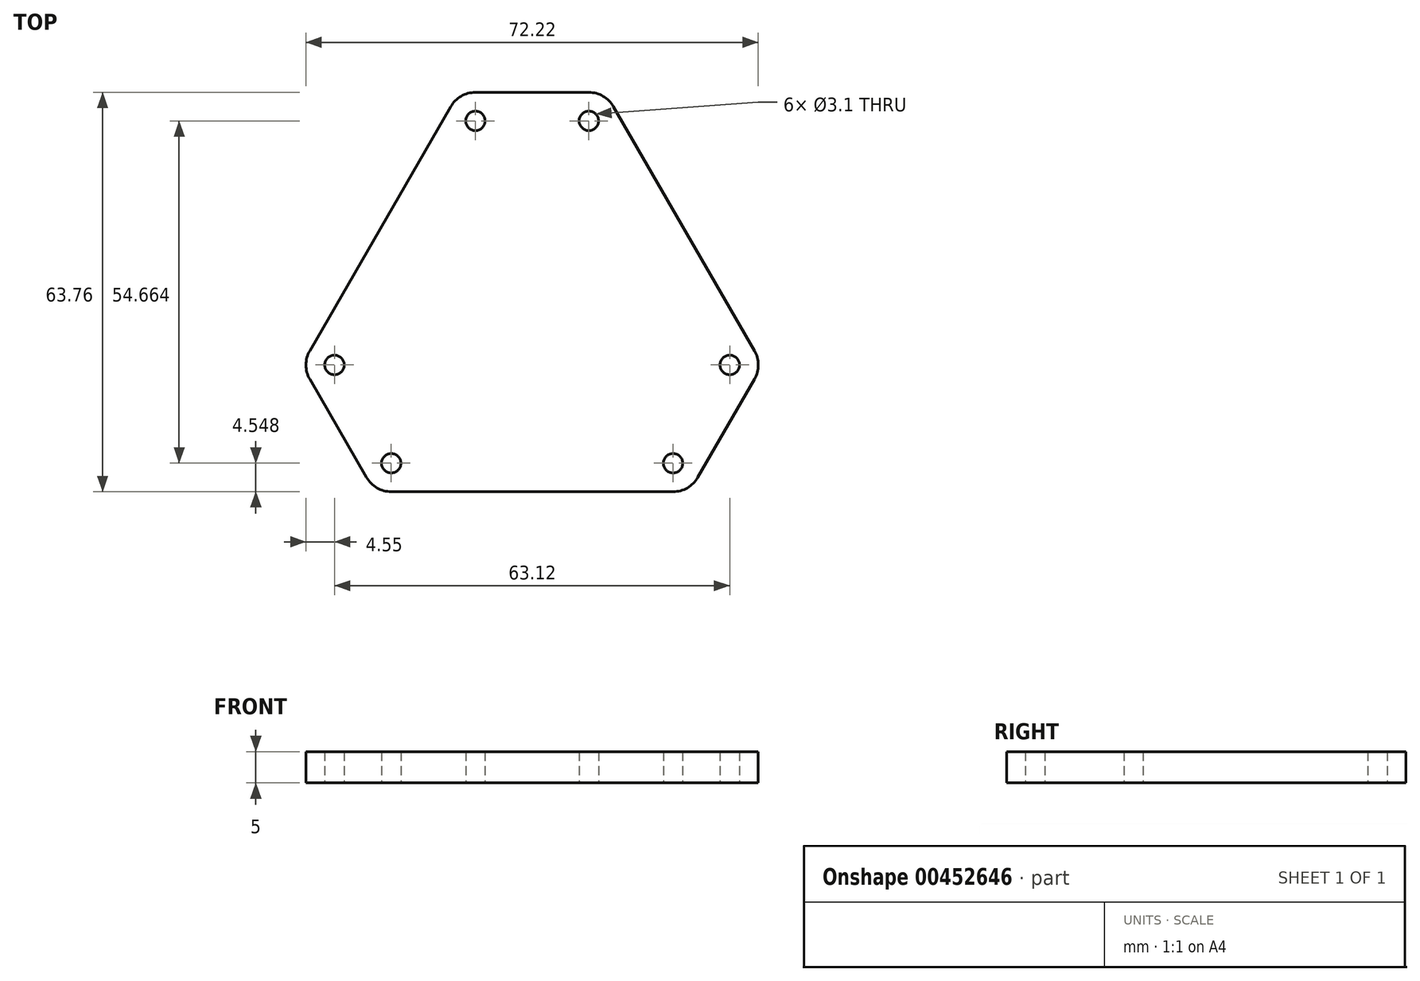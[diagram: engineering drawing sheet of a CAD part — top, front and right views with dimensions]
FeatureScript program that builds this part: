
annotation { "Feature Type Name" : "Feature", "Feature Type Description" : "" }
export const myFeature = defineFeature(function(context is Context, id is Id, definition is map)
    precondition{}
    {
        {
            var Q0;
            Q0=qCreatedBy(makeId("Top.planeOp"),FACE);
            var sketch = newSketch(context, id + "F0", { "sketchPlane" : qUnion([Q0])});
            skCircle(sketch, "E0", {"center": v(-22.5, -23.45) * mm, "radius": 1.55 * mm});
            skCircle(sketch, "E1", {"center": v(22.5, -23.45) * mm, "radius": 1.55 * mm});
            skLineSegment(sketch, "E2", {"start": v(-22.5, -23.45) * mm, "end": v(22.5, -23.45) * mm, "construction": true});
            skLineSegment(sketch, "E3", {"start": v(0, 0) * mm, "end": v(0, -23.45) * mm, "construction": true});
            skCircle(sketch, "E4", {"center": v(0, 0) * mm, "radius": 32.5 * mm, "construction": true});
            skLineSegment(sketch, "E5", {"start": v(-22.5, -28) * mm, "end": v(22.5, -28) * mm});
            skPoint(sketch, "E6.visualSharp", {"position": v(-33.76, -28) * mm});
            skPoint(sketch, "E7.visualSharp", {"position": v(33.76, -28) * mm});
            skArc(sketch, "E7.filletArc", {"start": v(22.5, -28) * mm, "mid": v(24.77, -27.4) * mm, "end": v(26.44, -25.73) * mm});
            skPoint(sketch, "E8.endSnap0", {"position": v(12.51, -10.17) * mm});
            skLineSegment(sketch, "E9", {"start": v(-26.44, -25.73) * mm, "end": v(-30.97, -17.88) * mm});
            skLineSegment(sketch, "E10", {"start": v(-30.97, -17.88) * mm, "end": v(0, 0) * mm});
            skLineSegment(sketch, "E11", {"start": v(0, 0) * mm, "end": v(30.97, -17.88) * mm});
            skLineSegment(sketch, "E12", {"start": v(30.97, -17.88) * mm, "end": v(26.44, -25.73) * mm});
            skPoint(sketch, "E12.endSnap0", {"position": v(26.44, -25.73) * mm});
            skArc(sketch, "E13.trimOffspring", {"start": v(-26.44, -25.73) * mm, "mid": v(-24.77, -27.4) * mm, "end": v(-22.5, -28) * mm});
            skSolve(sketch);
        }
        {
            var Q0;
            Q0=qSketchRegion(id+"F0",true);
            extrude(context, id + "F1", {"entities" : qUnion([Q0]), "depth" : 5 * mm});
        }
        {
            var Q0;
            Q0=makeQuery(id+"F1.opExtrude","SWEPT_BODY",BODY,{"disambiguationData":[OSD([sQuery(id+"F0.wireOp",EDGE,"E0"),sQuery(id+"F0.wireOp",EDGE,"E1"),sQuery(id+"F0.wireOp",EDGE,"E5"),sQuery(id+"F0.wireOp",EDGE,"E7.filletArc"),sQuery(id+"F0.wireOp",EDGE,"E9"),sQuery(id+"F0.wireOp",EDGE,"E10"),sQuery(id+"F0.wireOp",EDGE,"E11"),sQuery(id+"F0.wireOp",EDGE,"E12"),sQuery(id+"F0.wireOp",EDGE,"E13.trimOffspring")])]});
            var Q1;
            Q1=makeQuery(id+"F1.opExtrude","SWEPT_EDGE",EDGE,{"disambiguationData":[OSD([sQuery(id+"F0.wireOp",EDGE,"E10"),sQuery(id+"F0.wireOp",EDGE,"E11")])]});
            circularPattern(context, id + "F2", {"operationType" : NewBodyOperationType.ADD, "entities" : qUnion([Q0]), "axis" : qUnion([Q1]), "angle" : 120 * degree, "instanceCount" : 3});
        }
    });
